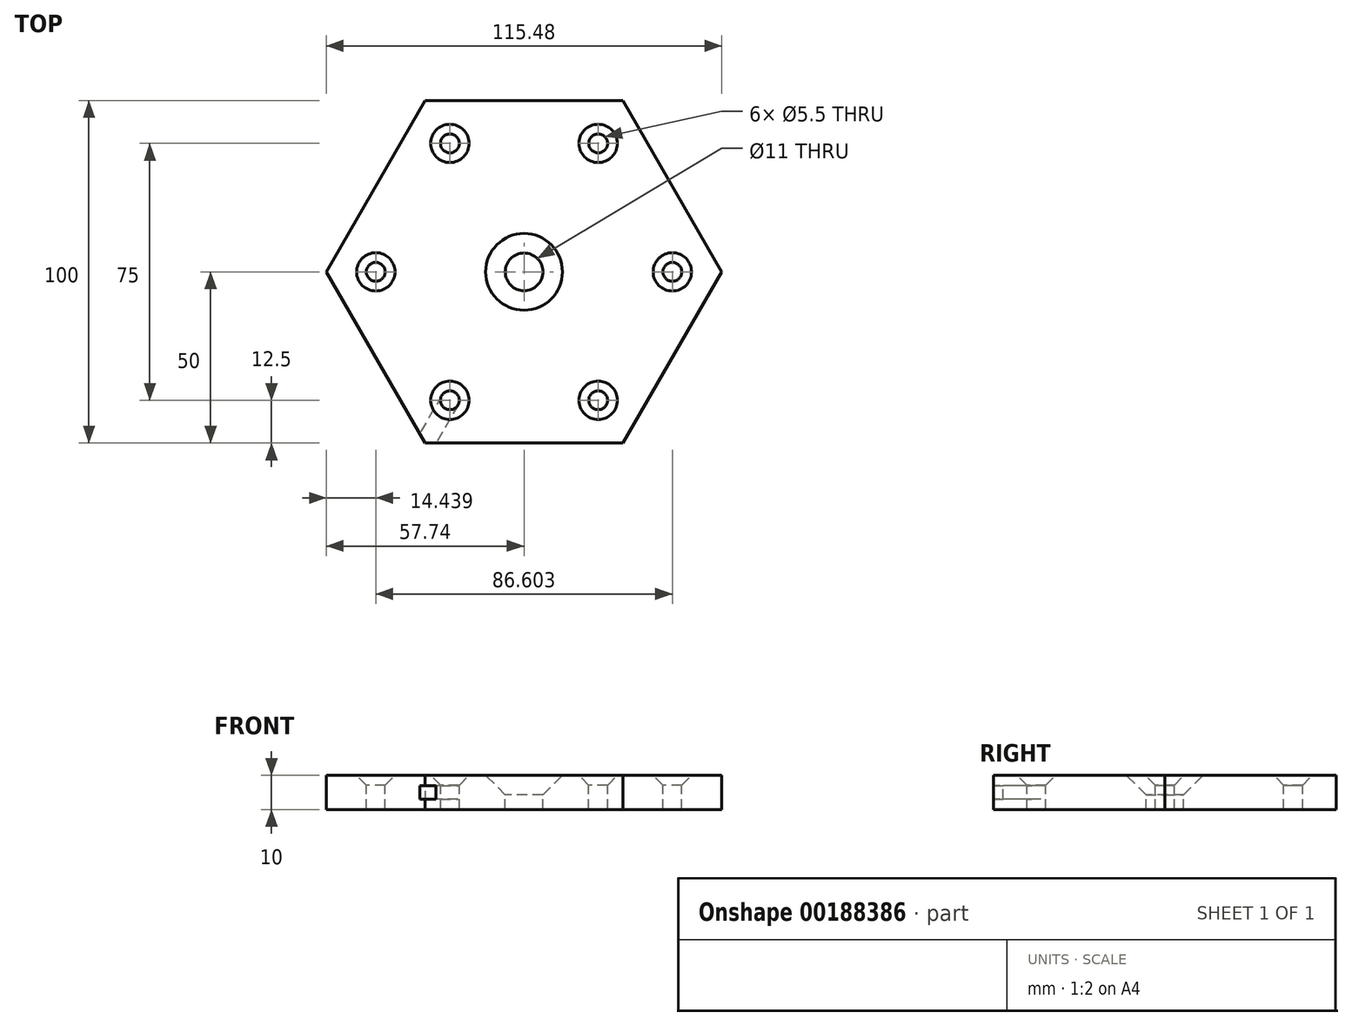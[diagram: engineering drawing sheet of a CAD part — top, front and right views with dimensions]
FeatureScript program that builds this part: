
annotation { "Feature Type Name" : "Feature", "Feature Type Description" : "" }
export const myFeature = defineFeature(function(context is Context, id is Id, definition is map)
    precondition{}
    {
        {
            var Q0;
            Q0=qCreatedBy(makeId("Top.planeOp"),FACE);
            var sketch = newSketch(context, id + "F0", { "sketchPlane" : qUnion([Q0])});
            skCircle(sketch, "E0.cCircle", {"center": v(0, 0) * mm, "radius": 50 * mm, "construction": true});
            skLineSegment(sketch, "E0.0", {"start": v(-28.87, 50) * mm, "end": v(28.87, 50) * mm});
            skLineSegment(sketch, "E0.1", {"start": v(28.87, 50) * mm, "end": v(57.74, 0) * mm});
            skLineSegment(sketch, "E0.2", {"start": v(57.74, 0) * mm, "end": v(28.87, -50) * mm});
            skLineSegment(sketch, "E0.3", {"start": v(28.87, -50) * mm, "end": v(-28.87, -50) * mm});
            skLineSegment(sketch, "E0.4", {"start": v(-28.87, -50) * mm, "end": v(-57.74, 0) * mm});
            skLineSegment(sketch, "E0.5", {"start": v(-57.74, 0) * mm, "end": v(-28.87, 50) * mm});
            skPoint(sketch, "E0.0.midPoint", {"position": v(0, 50) * mm});
            skLineSegment(sketch, "E1", {"start": v(0, 0) * mm, "end": v(0, 50) * mm, "construction": true});
            skLineSegment(sketch, "E2", {"start": v(0, 25) * mm, "end": v(0, 50) * mm, "construction": true});
            skPoint(sketch, "E3", {"position": v(0, 37.5) * mm});
            skSolve(sketch);
        }
        {
            var Q0;
            Q0 = qSketchRegion(id + "F0", true);
            extrude(context, id + "F1", {"entities" : qUnion([Q0]), "endBound" : BoundingType.SYMMETRIC, "depth" : 10 * mm});
        }
        {
            var Q0;
            Q0=makeQuery(id+"F1.opExtrude","CAP_FACE",FACE,{"disambiguationData":[OSD([sQuery(id+"F0.wireOp",EDGE,"E0.0"),sQuery(id+"F0.wireOp",EDGE,"E0.1"),sQuery(id+"F0.wireOp",EDGE,"E0.2"),sQuery(id+"F0.wireOp",EDGE,"E0.3"),sQuery(id+"F0.wireOp",EDGE,"E0.4"),sQuery(id+"F0.wireOp",EDGE,"E0.5")])],"isStart":false});
            var sketch = newSketch(context, id + "F2", { "sketchPlane" : qUnion([Q0])});
            skLineSegment(sketch, "E4", {"start": v(0, 0) * mm, "end": v(28.87, 50) * mm, "construction": true});
            skLineSegment(sketch, "E5", {"start": v(14.43, 25) * mm, "end": v(28.87, 50) * mm, "construction": true});
            skPoint(sketch, "E6", {"position": v(21.65, 37.5) * mm});
            skCircle(sketch, "E7", {"center": v(0, 0) * mm, "radius": 43.3 * mm, "construction": true});
            skLineSegment(sketch, "E8.1.0", {"start": v(57.74, 0) * mm, "end": v(0, 0) * mm, "construction": true});
            skLineSegment(sketch, "E8.2.0", {"start": v(0, 0) * mm, "end": v(28.87, -50) * mm, "construction": true});
            skLineSegment(sketch, "E8.3.0", {"start": v(0, 0) * mm, "end": v(-28.87, -50) * mm, "construction": true});
            skLineSegment(sketch, "E8.4.0", {"start": v(-57.74, 0) * mm, "end": v(0, 0) * mm, "construction": true});
            skLineSegment(sketch, "E8.5.0", {"start": v(0, 0) * mm, "end": v(-28.87, 50) * mm, "construction": true});
            skPoint(sketch, "E9", {"position": v(43.3, 0) * mm});
            skPoint(sketch, "E10", {"position": v(-21.65, -37.5) * mm});
            skPoint(sketch, "E11", {"position": v(-21.65, 37.5) * mm});
            skPoint(sketch, "E12", {"position": v(-43.3, 0) * mm});
            skPoint(sketch, "E13", {"position": v(21.65, -37.5) * mm});
            skSolve(sketch);
        }
        {
            var Q0;
            Q0=makeQuery(id+"F1.opExtrude","CAP_FACE",FACE,{"disambiguationData":[OSD([sQuery(id+"F0.wireOp",EDGE,"E0.0"),sQuery(id+"F0.wireOp",EDGE,"E0.1"),sQuery(id+"F0.wireOp",EDGE,"E0.2"),sQuery(id+"F0.wireOp",EDGE,"E0.3"),sQuery(id+"F0.wireOp",EDGE,"E0.4"),sQuery(id+"F0.wireOp",EDGE,"E0.5")])],"isStart":false});
            var sketch = newSketch(context, id + "F3", { "sketchPlane" : qUnion([Q0])});
            skPoint(sketch, "E14", {"position": v(0, 0) * mm});
            skSolve(sketch);
        }
        {
            var Q0;
            Q0=sQuery(id+"F3.wireOp",VERTEX,"E14");
            var Q1;
            Q1=makeQuery(id+"F1.opExtrude","SWEPT_BODY",BODY,{"disambiguationData":[OSD([sQuery(id+"F0.wireOp",EDGE,"E0.0"),sQuery(id+"F0.wireOp",EDGE,"E0.1"),sQuery(id+"F0.wireOp",EDGE,"E0.2"),sQuery(id+"F0.wireOp",EDGE,"E0.3"),sQuery(id+"F0.wireOp",EDGE,"E0.4"),sQuery(id+"F0.wireOp",EDGE,"E0.5")])]});
            hole(context, id + "F4", {"style" : HoleStyle.C_SINK, "endStyle" : HoleEndStyle.BLIND, "standardTappedOrClearance" : lookupTablePath({ "standard" : "ISO", "fit" : "Normal", "size" : "M10", "type" : "Clearance" }), "standardBlindInLast" : lookupTablePath({ "fit" : "Standard", "standard" : "ISO", "size" : "M10", "type" : "Clearance" }), "holeDiameter" : 11 * mm, "cSinkDiameter" : 22.4 * mm, "cSinkAngle" : 90 * degree, "holeDepth" : 57.15 * mm, "locations" : qUnion([Q0]), "scope" : qUnion([Q1])});
        }
        {
            var Q0;
            Q0=sQuery(id+"F2.wireOp",VERTEX,"E6");
            var Q1;
            Q1=sQuery(id+"F2.wireOp",VERTEX,"E9");
            var Q2;
            Q2=sQuery(id+"F2.wireOp",VERTEX,"E13");
            var Q3;
            Q3=sQuery(id+"F2.wireOp",VERTEX,"E10");
            var Q4;
            Q4=sQuery(id+"F2.wireOp",VERTEX,"E12");
            var Q5;
            Q5=sQuery(id+"F2.wireOp",VERTEX,"E11");
            var Q6;
            Q6=makeQuery(id+"F1.opExtrude","SWEPT_BODY",BODY,{"disambiguationData":[OSD([sQuery(id+"F0.wireOp",EDGE,"E0.0"),sQuery(id+"F0.wireOp",EDGE,"E0.1"),sQuery(id+"F0.wireOp",EDGE,"E0.2"),sQuery(id+"F0.wireOp",EDGE,"E0.3"),sQuery(id+"F0.wireOp",EDGE,"E0.4"),sQuery(id+"F0.wireOp",EDGE,"E0.5")])]});
            hole(context, id + "F5", {"style" : HoleStyle.C_SINK, "endStyle" : HoleEndStyle.BLIND, "standardTappedOrClearance" : lookupTablePath({ "standard" : "ISO", "fit" : "Normal", "size" : "M5", "type" : "Clearance" }), "standardBlindInLast" : lookupTablePath({ "fit" : "Standard", "standard" : "ISO", "size" : "M5", "type" : "Clearance" }), "holeDiameter" : 5.5 * mm, "cSinkDiameter" : 11.2 * mm, "cSinkAngle" : 90 * degree, "holeDepth" : 57.15 * mm, "locations" : qUnion([Q0, Q1, Q2, Q3, Q4, Q5]), "scope" : qUnion([Q6])});
        }
        {
            var Q0;
            Q0=qCreatedBy(makeId("Top.planeOp"),FACE);
            var sketch = newSketch(context, id + "F6", { "sketchPlane" : qUnion([Q0])});
            skCircle(sketch, "E15.0", {"center": v(-21.65, -37.5) * mm, "radius": 2.75 * mm});
            skLineSegment(sketch, "E16", {"start": v(-24.03, -36.12) * mm, "end": v(-30.46, -47.25) * mm});
            skLineSegment(sketch, "E17", {"start": v(-19.27, -38.87) * mm, "end": v(-25.7, -50) * mm});
            skLineSegment(sketch, "E18.0", {"start": v(28.87, -50) * mm, "end": v(-28.87, -50) * mm});
            skLineSegment(sketch, "E19.0", {"start": v(-28.87, -50) * mm, "end": v(-57.74, 0) * mm});
            skLineSegment(sketch, "E20", {"start": v(-21.65, -37.5) * mm, "end": v(-28.87, -50) * mm, "construction": true});
            skSolve(sketch);
        }
        {
            var Q0;
            Q0 = qSketchRegion(id + "F6", true);
            extrude(context, id + "F7", {"entities" : qUnion([Q0]), "operationType" : NewBodyOperationType.REMOVE, "endBound" : BoundingType.SYMMETRIC, "oppositeDirection" : true, "depth" : 4 * mm});
        }
    });
